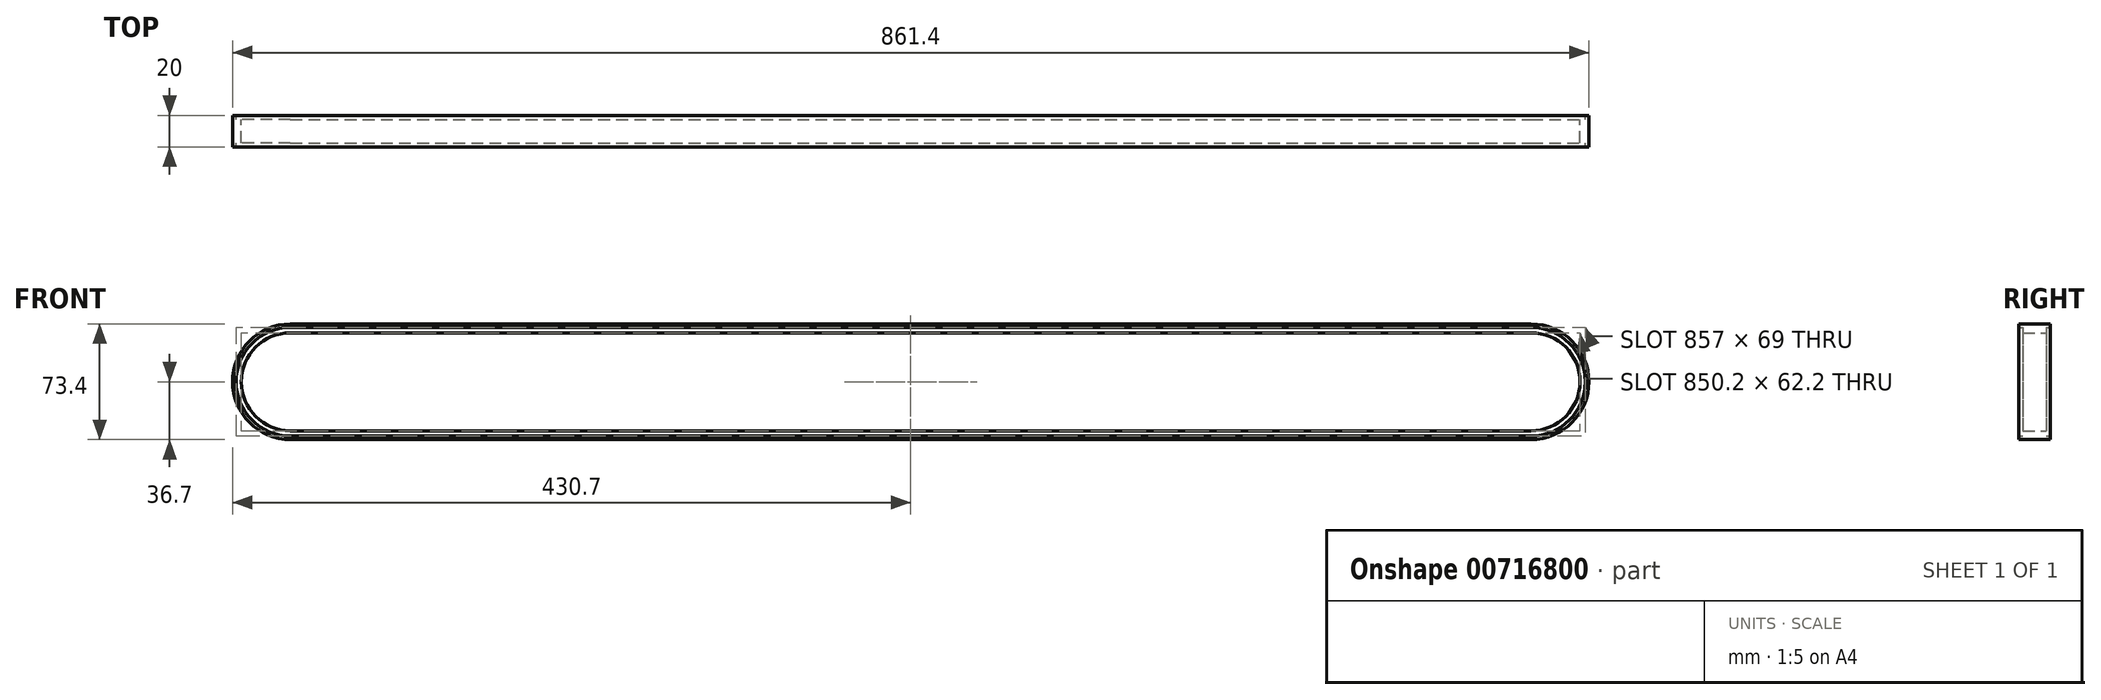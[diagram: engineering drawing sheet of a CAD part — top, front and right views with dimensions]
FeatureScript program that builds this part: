
annotation { "Feature Type Name" : "Feature", "Feature Type Description" : "" }
export const myFeature = defineFeature(function(context is Context, id is Id, definition is map)
    precondition{}
    {
        {
            var Q0;
            Q0=qCreatedBy(makeId("Front.planeOp"),FACE);
            var sketch = newSketch(context, id + "F0", { "sketchPlane" : qUnion([Q0])});
            skLineSegment(sketch, "E0", {"start": v(-394, 0) * mm, "end": v(394, 0) * mm});
            skArc(sketch, "E1.0.startCap", {"start": v(-394, -34.5) * mm, "mid": v(-428.5, 0) * mm, "end": v(-394, 34.5) * mm});
            skArc(sketch, "E1.0.endCap", {"start": v(394, 34.5) * mm, "mid": v(428.5, 0) * mm, "end": v(394, -34.5) * mm});
            skLineSegment(sketch, "E1.0.left", {"start": v(-394, 34.5) * mm, "end": v(394, 34.5) * mm});
            skLineSegment(sketch, "E1.0.right", {"start": v(-394, -34.5) * mm, "end": v(394, -34.5) * mm});
            skLineSegment(sketch, "E2.0", {"start": v(-394, 36.7) * mm, "end": v(394, 36.7) * mm});
            skArc(sketch, "E2.1", {"start": v(-394, -36.7) * mm, "mid": v(-430.7, 0) * mm, "end": v(-394, 36.7) * mm});
            skLineSegment(sketch, "E2.2", {"start": v(-394, -36.7) * mm, "end": v(394, -36.7) * mm});
            skArc(sketch, "E2.3", {"start": v(394, 36.7) * mm, "mid": v(430.7, 0) * mm, "end": v(394, -36.7) * mm});
            skSolve(sketch);
        }
        {
            var Q0;
            Q0 = qSketchRegion(id + "F0", true);
            extrude(context, id + "F1", {"entities" : qUnion([Q0]), "endBound" : BoundingType.SYMMETRIC, "depth" : 20 * mm, "offsetDistance" : 25 * mm});
        }
        {
            var Q0;
            Q0=qCreatedBy(makeId("Front.planeOp"),FACE);
            var sketch = newSketch(context, id + "F2", { "sketchPlane" : qUnion([Q0])});
            skLineSegment(sketch, "E3.0", {"start": v(-394, 31.1) * mm, "end": v(394, 31.1) * mm});
            skArc(sketch, "E3.1", {"start": v(-394, -31.1) * mm, "mid": v(-425.1, 0) * mm, "end": v(-394, 31.1) * mm});
            skLineSegment(sketch, "E3.2", {"start": v(-394, -31.1) * mm, "end": v(394, -31.1) * mm});
            skArc(sketch, "E3.3", {"start": v(394, 31.1) * mm, "mid": v(425.1, 0) * mm, "end": v(394, -31.1) * mm});
            skLineSegment(sketch, "E4.0", {"start": v(-394, 34.5) * mm, "end": v(394, 34.5) * mm});
            skArc(sketch, "E5.0", {"start": v(-394, -34.5) * mm, "mid": v(-428.5, 0) * mm, "end": v(-394, 34.5) * mm});
            skLineSegment(sketch, "E6.0", {"start": v(-394, -34.5) * mm, "end": v(394, -34.5) * mm});
            skArc(sketch, "E7.0", {"start": v(394, 34.5) * mm, "mid": v(428.5, 0) * mm, "end": v(394, -34.5) * mm});
            skSolve(sketch);
        }
        {
            var Q0;
            Q0 = qSketchRegion(id + "F2", true);
            extrude(context, id + "F3", {"entities" : qUnion([Q0]), "operationType" : NewBodyOperationType.ADD, "endBound" : BoundingType.SYMMETRIC, "depth" : 15 * mm, "offsetDistance" : 25 * mm});
        }
    });
